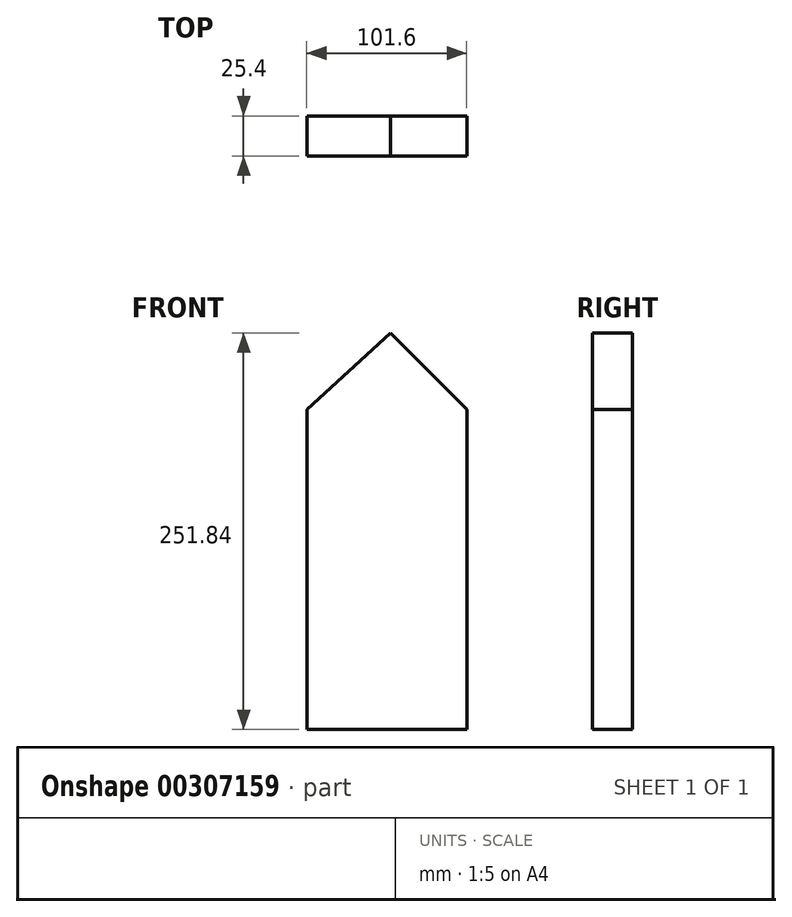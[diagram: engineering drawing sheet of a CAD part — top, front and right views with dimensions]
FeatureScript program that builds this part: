
annotation { "Feature Type Name" : "Feature", "Feature Type Description" : "" }
export const myFeature = defineFeature(function(context is Context, id is Id, definition is map)
    precondition{}
    {
        {
            var Q0;
            Q0=qCreatedBy(makeId("Front.planeOp"),FACE);
            var sketch = newSketch(context, id + "F0", { "sketchPlane" : qUnion([Q0])});
            skLineSegment(sketch, "E0.bottom", {"start": v(-101.46, 73.5) * mm, "end": v(0.14, 73.5) * mm});
            skLineSegment(sketch, "E0.top", {"start": v(-101.46, -129.7) * mm, "end": v(0.14, -129.7) * mm});
            skLineSegment(sketch, "E0.left", {"start": v(-101.46, 73.5) * mm, "end": v(-101.46, -129.7) * mm});
            skLineSegment(sketch, "E0.right", {"start": v(0.14, 73.5) * mm, "end": v(0.14, -129.7) * mm});
            skLineSegment(sketch, "E1", {"start": v(-101.46, 73.5) * mm, "end": v(-48.32, 122.14) * mm});
            skLineSegment(sketch, "E2", {"start": v(-48.32, 122.14) * mm, "end": v(0.14, 73.5) * mm});
            skSolve(sketch);
        }
        {
            var Q0;
            Q0=makeQuery(id+"F0.imprint","IMPRINT",FACE,{"disambiguationData":[TD([[makeQuery(id+"F0.imprint","IMPRINT",EDGE,{"derivedFrom":sQuery(id+"F0.wireOp",EDGE,"E0.bottom")}),-1.0]])]});
            extrude(context, id + "F1", {"entities" : qUnion([Q0]), "depth" : 25.4 * mm});
        }
        {
            var Q0;
            Q0=makeQuery(id+"F0.imprint","IMPRINT",FACE,{"disambiguationData":[TD([[makeQuery(id+"F0.imprint","IMPRINT",EDGE,{"derivedFrom":sQuery(id+"F0.wireOp",EDGE,"E0.bottom")}),1.0]])]});
            extrude(context, id + "F2", {"entities" : qUnion([Q0]), "operationType" : NewBodyOperationType.ADD, "depth" : 25.4 * mm});
        }
    });
